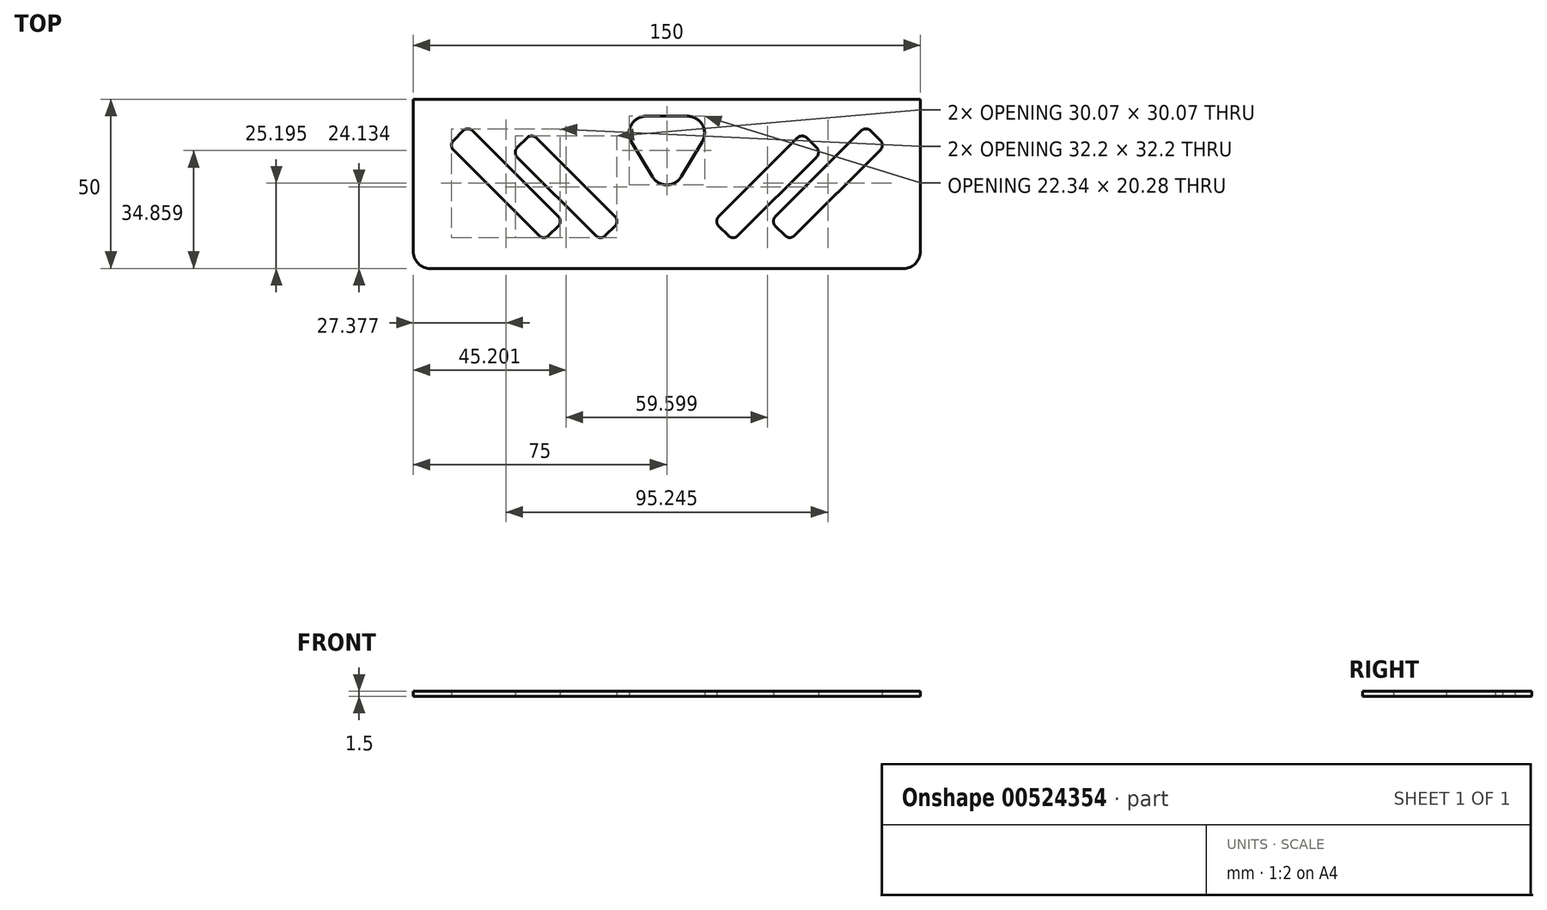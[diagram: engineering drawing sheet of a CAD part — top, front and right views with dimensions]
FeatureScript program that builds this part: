
annotation { "Feature Type Name" : "Feature", "Feature Type Description" : "" }
export const myFeature = defineFeature(function(context is Context, id is Id, definition is map)
    precondition{}
    {
        {
            var Q0;
            Q0=qCreatedBy(makeId("Top.planeOp"),FACE);
            var sketch = newSketch(context, id + "F0", { "sketchPlane" : qUnion([Q0])});
            skLineSegment(sketch, "E0.bottom", {"start": v(5, 0) * mm, "end": v(145, 0) * mm});
            skLineSegment(sketch, "E0.top", {"start": v(0, 50) * mm, "end": v(150, 50) * mm});
            skLineSegment(sketch, "E0.left", {"start": v(0, 5) * mm, "end": v(0, 50) * mm});
            skLineSegment(sketch, "E0.right", {"start": v(150, 5) * mm, "end": v(150, 50) * mm});
            skLineSegment(sketch, "E1.top", {"start": v(81.17, 45) * mm, "end": v(68.83, 45) * mm});
            skLineSegment(sketch, "E2", {"start": v(64.54, 37.43) * mm, "end": v(70.71, 27.15) * mm});
            skLineSegment(sketch, "E3", {"start": v(79.29, 27.15) * mm, "end": v(85.46, 37.43) * mm});
            skPoint(sketch, "E4.visualSharp", {"position": v(60, 45) * mm});
            skArc(sketch, "E4.filletArc", {"start": v(68.83, 45) * mm, "mid": v(64.48, 42.46) * mm, "end": v(64.54, 37.43) * mm});
            skPoint(sketch, "E5.visualSharp", {"position": v(90, 45) * mm});
            skArc(sketch, "E5.filletArc", {"start": v(85.46, 37.43) * mm, "mid": v(85.52, 42.46) * mm, "end": v(81.17, 45) * mm});
            skPoint(sketch, "E6.visualSharp", {"position": v(75, 20) * mm});
            skArc(sketch, "E6.filletArc", {"start": v(70.71, 27.15) * mm, "mid": v(75, 24.72) * mm, "end": v(79.29, 27.15) * mm});
            skLineSegment(sketch, "E7.bottom", {"start": v(36.41, 38.59) * mm, "end": v(59.65, 15.35) * mm});
            skLineSegment(sketch, "E7.top", {"start": v(30.75, 32.92) * mm, "end": v(53.99, 9.68) * mm});
            skLineSegment(sketch, "E7.left", {"start": v(33.59, 38.59) * mm, "end": v(30.75, 35.75) * mm});
            skLineSegment(sketch, "E7.right", {"start": v(59.65, 12.52) * mm, "end": v(56.82, 9.68) * mm});
            skLineSegment(sketch, "E8", {"start": v(0, 50) * mm, "end": v(0, -8.06) * mm, "construction": true});
            skLineSegment(sketch, "E9.bottom", {"start": v(17.53, 40.7) * mm, "end": v(42.89, 15.35) * mm});
            skLineSegment(sketch, "E9.top", {"start": v(11.87, 35.04) * mm, "end": v(37.22, 9.68) * mm});
            skLineSegment(sketch, "E9.left", {"start": v(14.7, 40.7) * mm, "end": v(11.87, 37.87) * mm});
            skLineSegment(sketch, "E9.right", {"start": v(42.89, 12.52) * mm, "end": v(40.05, 9.68) * mm});
            skLineSegment(sketch, "E10", {"start": v(75, 50) * mm, "end": v(75, 0) * mm, "construction": true});
            skLineSegment(sketch, "E11.MirrorCS", {"start": v(25, 0) * mm, "end": v(75, 0) * mm, "construction": true});
            skLineSegment(sketch, "E12.MirrorCS", {"start": v(113.59, 38.59) * mm, "end": v(90.35, 15.35) * mm});
            skLineSegment(sketch, "E13.MirrorCS", {"start": v(90.35, 12.52) * mm, "end": v(93.18, 9.68) * mm});
            skLineSegment(sketch, "E14.MirrorCS", {"start": v(119.25, 32.92) * mm, "end": v(96.01, 9.68) * mm});
            skLineSegment(sketch, "E15.MirrorCS", {"start": v(116.41, 38.59) * mm, "end": v(119.25, 35.75) * mm});
            skLineSegment(sketch, "E16.MirrorCS", {"start": v(132.47, 40.7) * mm, "end": v(107.11, 15.35) * mm});
            skLineSegment(sketch, "E17.MirrorCS", {"start": v(135.3, 40.7) * mm, "end": v(138.13, 37.87) * mm});
            skLineSegment(sketch, "E18.MirrorCS", {"start": v(138.13, 35.04) * mm, "end": v(112.78, 9.68) * mm});
            skLineSegment(sketch, "E19.MirrorCS", {"start": v(107.11, 12.52) * mm, "end": v(109.95, 9.68) * mm});
            skPoint(sketch, "E20.visualSharp", {"position": v(0, 0) * mm});
            skArc(sketch, "E20.filletArc", {"start": v(0, 5) * mm, "mid": v(1.46, 1.46) * mm, "end": v(5, 0) * mm});
            skPoint(sketch, "E21.visualSharp", {"position": v(150, 0) * mm});
            skArc(sketch, "E21.filletArc", {"start": v(145, 0) * mm, "mid": v(148.54, 1.46) * mm, "end": v(150, 5) * mm});
            skPoint(sketch, "E22.visualSharp", {"position": v(35, 40) * mm});
            skArc(sketch, "E22.filletArc", {"start": v(36.41, 38.59) * mm, "mid": v(35, 39.17) * mm, "end": v(33.59, 38.59) * mm});
            skPoint(sketch, "E23.visualSharp", {"position": v(55.4, 8.27) * mm});
            skArc(sketch, "E23.filletArc", {"start": v(53.99, 9.68) * mm, "mid": v(55.4, 9.1) * mm, "end": v(56.82, 9.68) * mm});
            skPoint(sketch, "E24.visualSharp", {"position": v(29.33, 34.33) * mm});
            skArc(sketch, "E24.filletArc", {"start": v(30.75, 35.75) * mm, "mid": v(30.16, 34.33) * mm, "end": v(30.75, 32.92) * mm});
            skPoint(sketch, "E25.visualSharp", {"position": v(61.07, 13.93) * mm});
            skArc(sketch, "E25.filletArc", {"start": v(59.65, 12.52) * mm, "mid": v(60.24, 13.93) * mm, "end": v(59.65, 15.35) * mm});
            skPoint(sketch, "E26.visualSharp", {"position": v(16.12, 42.12) * mm});
            skArc(sketch, "E26.filletArc", {"start": v(17.53, 40.7) * mm, "mid": v(16.12, 41.3) * mm, "end": v(14.7, 40.7) * mm});
            skPoint(sketch, "E27.visualSharp", {"position": v(10.45, 36.46) * mm});
            skArc(sketch, "E27.filletArc", {"start": v(11.87, 37.87) * mm, "mid": v(11.28, 36.46) * mm, "end": v(11.87, 35.04) * mm});
            skPoint(sketch, "E28.visualSharp", {"position": v(38.64, 8.27) * mm});
            skArc(sketch, "E28.filletArc", {"start": v(37.22, 9.68) * mm, "mid": v(38.64, 9.1) * mm, "end": v(40.05, 9.68) * mm});
            skPoint(sketch, "E29.visualSharp", {"position": v(44.3, 13.93) * mm});
            skArc(sketch, "E29.filletArc", {"start": v(42.89, 12.52) * mm, "mid": v(43.48, 13.93) * mm, "end": v(42.89, 15.35) * mm});
            skPoint(sketch, "E30.visualSharp", {"position": v(115, 40) * mm});
            skArc(sketch, "E30.filletArc", {"start": v(116.41, 38.59) * mm, "mid": v(115, 39.17) * mm, "end": v(113.59, 38.59) * mm});
            skPoint(sketch, "E31.visualSharp", {"position": v(88.93, 13.93) * mm});
            skArc(sketch, "E31.filletArc", {"start": v(90.35, 15.35) * mm, "mid": v(89.76, 13.93) * mm, "end": v(90.35, 12.52) * mm});
            skPoint(sketch, "E32.visualSharp", {"position": v(94.6, 8.27) * mm});
            skArc(sketch, "E32.filletArc", {"start": v(93.18, 9.68) * mm, "mid": v(94.6, 9.1) * mm, "end": v(96.01, 9.68) * mm});
            skPoint(sketch, "E33.visualSharp", {"position": v(105.7, 13.93) * mm});
            skArc(sketch, "E33.filletArc", {"start": v(107.11, 15.35) * mm, "mid": v(106.52, 13.93) * mm, "end": v(107.11, 12.52) * mm});
            skPoint(sketch, "E34.visualSharp", {"position": v(111.36, 8.27) * mm});
            skArc(sketch, "E34.filletArc", {"start": v(109.95, 9.68) * mm, "mid": v(111.36, 9.1) * mm, "end": v(112.78, 9.68) * mm});
            skPoint(sketch, "E35.visualSharp", {"position": v(139.55, 36.46) * mm});
            skArc(sketch, "E35.filletArc", {"start": v(138.13, 35.04) * mm, "mid": v(138.72, 36.46) * mm, "end": v(138.13, 37.87) * mm});
            skPoint(sketch, "E36.visualSharp", {"position": v(133.88, 42.12) * mm});
            skArc(sketch, "E36.filletArc", {"start": v(135.3, 40.7) * mm, "mid": v(133.88, 41.3) * mm, "end": v(132.47, 40.7) * mm});
            skPoint(sketch, "E37.visualSharp", {"position": v(120.67, 34.33) * mm});
            skArc(sketch, "E37.filletArc", {"start": v(119.25, 32.92) * mm, "mid": v(119.84, 34.33) * mm, "end": v(119.25, 35.75) * mm});
            skSolve(sketch);
        }
        {
            var Q0;
            Q0=makeQuery(id+"F0.imprint","IMPRINT",FACE,{"disambiguationData":[TD([[makeQuery(id+"F0.imprint","IMPRINT",EDGE,{"derivedFrom":sQuery(id+"F0.wireOp",EDGE,"E0.bottom")}),1.0]])]});
            extrude(context, id + "F1", {"entities" : qUnion([Q0]), "depth" : 1.5 * mm, "offsetDistance" : 25 * mm});
        }
    });
